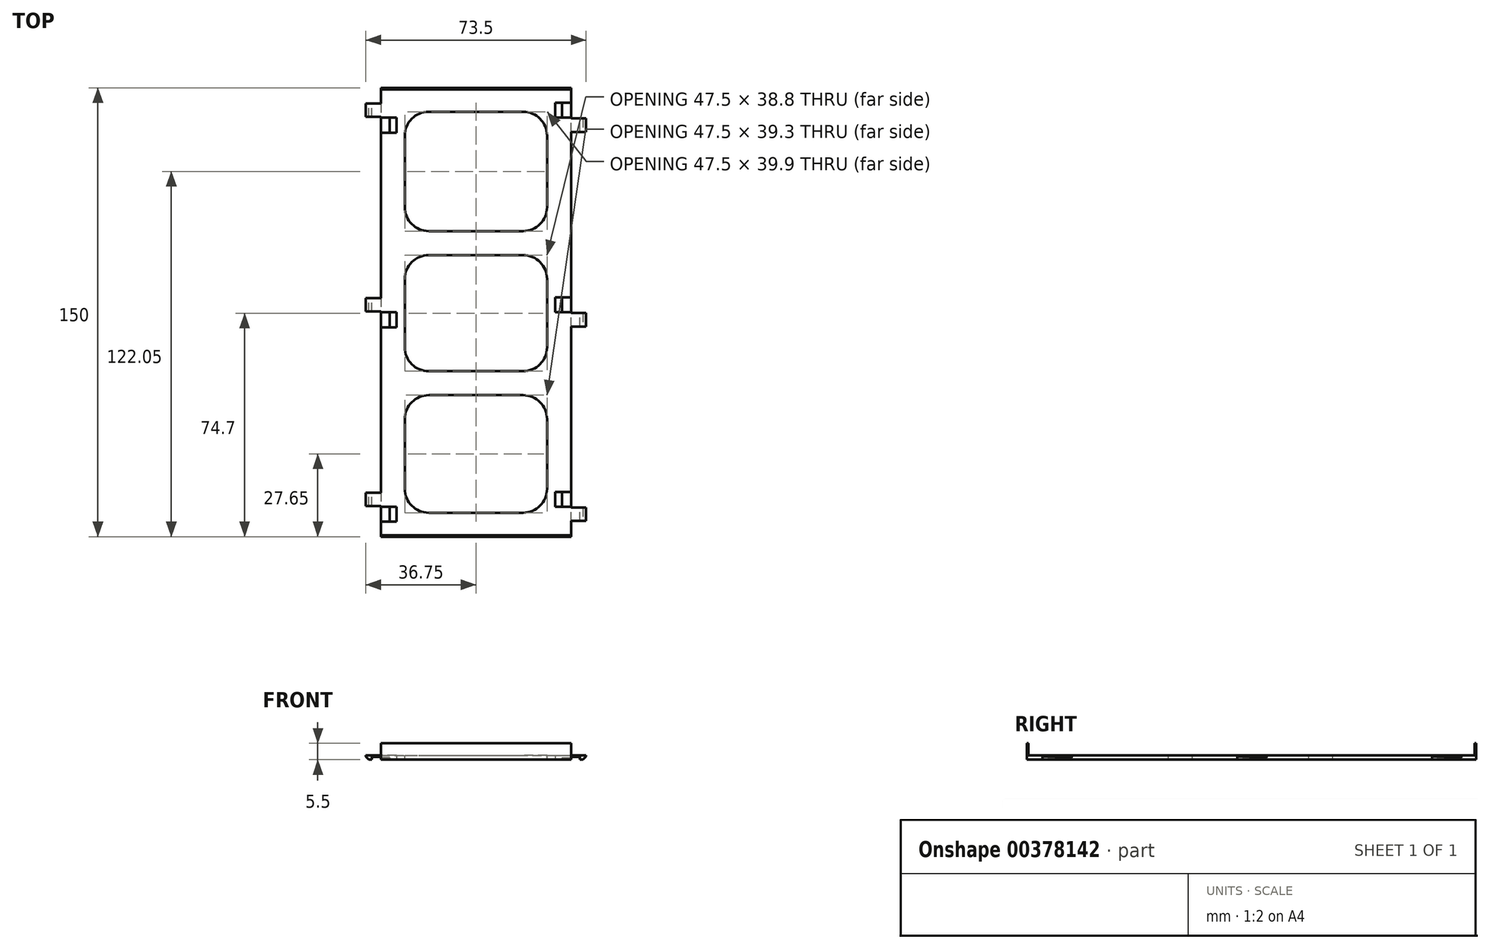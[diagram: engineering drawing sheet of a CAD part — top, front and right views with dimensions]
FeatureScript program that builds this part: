
annotation { "Feature Type Name" : "Feature", "Feature Type Description" : "" }
export const myFeature = defineFeature(function(context is Context, id is Id, definition is map)
    precondition{}
    {
        {
            var Q0;
            Q0=qCreatedBy(makeId("Top.planeOp"),FACE);
            var sketch = newSketch(context, id + "F0", { "sketchPlane" : qUnion([Q0])});
            skLineSegment(sketch, "E0.bottom", {"start": v(0, 0) * mm, "end": v(63.5, 0) * mm});
            skLineSegment(sketch, "E0.top", {"start": v(0, 150) * mm, "end": v(63.5, 150) * mm});
            skLineSegment(sketch, "E0.left", {"start": v(0, 0) * mm, "end": v(0, 150) * mm});
            skLineSegment(sketch, "E0.right", {"start": v(63.5, 0) * mm, "end": v(63.5, 150) * mm});
            skSolve(sketch);
        }
        {
            var Q0;
            Q0=qSketchRegion(id+"F0",true);
            extrude(context, id + "F1", {"entities" : qUnion([Q0]), "depth" : 1.5 * mm});
        }
        {
            var Q0;
            Q0=makeQuery(id+"F1.opExtrude","CAP_FACE",FACE,{"disambiguationData":[OSD([sQuery(id+"F0.wireOp",EDGE,"E0.bottom"),sQuery(id+"F0.wireOp",EDGE,"E0.top"),sQuery(id+"F0.wireOp",EDGE,"E0.left"),sQuery(id+"F0.wireOp",EDGE,"E0.right")])],"isStart":false});
            var sketch = newSketch(context, id + "F2", { "sketchPlane" : qUnion([Q0])});
            skLineSegment(sketch, "E1.bottom", {"start": v(8, 8) * mm, "end": v(55.5, 8) * mm});
            skLineSegment(sketch, "E1.top", {"start": v(8, 47.3) * mm, "end": v(55.5, 47.3) * mm});
            skLineSegment(sketch, "E1.left", {"start": v(8, 8) * mm, "end": v(8, 47.3) * mm});
            skLineSegment(sketch, "E1.right", {"start": v(55.5, 8) * mm, "end": v(55.5, 47.3) * mm});
            skLineSegment(sketch, "E2.bottom", {"start": v(8, 142) * mm, "end": v(55.5, 142) * mm});
            skLineSegment(sketch, "E2.top", {"start": v(8, 102.1) * mm, "end": v(55.5, 102.1) * mm});
            skLineSegment(sketch, "E2.left", {"start": v(8, 142) * mm, "end": v(8, 102.1) * mm});
            skLineSegment(sketch, "E2.right", {"start": v(55.5, 142) * mm, "end": v(55.5, 102.1) * mm});
            skLineSegment(sketch, "E3.bottom", {"start": v(8, 94.1) * mm, "end": v(55.5, 94.1) * mm});
            skLineSegment(sketch, "E3.top", {"start": v(8, 55.3) * mm, "end": v(55.5, 55.3) * mm});
            skLineSegment(sketch, "E3.left", {"start": v(8, 94.1) * mm, "end": v(8, 55.3) * mm});
            skLineSegment(sketch, "E3.right", {"start": v(55.5, 94.1) * mm, "end": v(55.5, 55.3) * mm});
            skSolve(sketch);
        }
        {
            var Q0;
            Q0=makeQuery(id+"F2.imprint","IMPRINT",FACE,{"disambiguationData":[TD([[makeQuery(id+"F2.imprint","IMPRINT",EDGE,{"derivedFrom":sQuery(id+"F2.wireOp",EDGE,"E2.bottom")}),-1.0]])]});
            var Q1;
            Q1=makeQuery(id+"F2.imprint","IMPRINT",FACE,{"disambiguationData":[TD([[makeQuery(id+"F2.imprint","IMPRINT",EDGE,{"derivedFrom":sQuery(id+"F2.wireOp",EDGE,"E3.bottom")}),-1.0]])]});
            var Q2;
            Q2=makeQuery(id+"F2.imprint","IMPRINT",FACE,{"disambiguationData":[TD([[makeQuery(id+"F2.imprint","IMPRINT",EDGE,{"derivedFrom":sQuery(id+"F2.wireOp",EDGE,"E1.bottom")}),1.0]])]});
            extrude(context, id + "F3", {"entities" : qUnion([Q0, Q1, Q2]), "operationType" : NewBodyOperationType.REMOVE, "endBound" : BoundingType.THROUGH_ALL, "oppositeDirection" : true, "depth" : 25 * mm});
        }
        {
            var Q0;
            Q0=makeQuery(id+"F3.boolean.opBoolean","COPY",EDGE,{"derivedFrom":makeQuery(id+"F3.opExtrude","SWEPT_EDGE",EDGE,{"disambiguationData":[OSD([sQuery(id+"F2.wireOp",EDGE,"E2.bottom"),sQuery(id+"F2.wireOp",EDGE,"E2.left")])]})});
            var Q1;
            Q1=makeQuery(id+"F3.boolean.opBoolean","COPY",EDGE,{"derivedFrom":makeQuery(id+"F3.opExtrude","SWEPT_EDGE",EDGE,{"disambiguationData":[OSD([sQuery(id+"F2.wireOp",EDGE,"E3.bottom"),sQuery(id+"F2.wireOp",EDGE,"E3.left")])]})});
            var Q2;
            Q2=makeQuery(id+"F3.boolean.opBoolean","COPY",EDGE,{"derivedFrom":makeQuery(id+"F3.opExtrude","SWEPT_EDGE",EDGE,{"disambiguationData":[OSD([sQuery(id+"F2.wireOp",EDGE,"E1.top"),sQuery(id+"F2.wireOp",EDGE,"E1.left")])]})});
            var Q3;
            Q3=makeQuery(id+"F3.boolean.opBoolean","COPY",EDGE,{"derivedFrom":makeQuery(id+"F3.opExtrude","SWEPT_EDGE",EDGE,{"disambiguationData":[OSD([sQuery(id+"F2.wireOp",EDGE,"E2.top"),sQuery(id+"F2.wireOp",EDGE,"E2.left")])]})});
            var Q4;
            Q4=makeQuery(id+"F3.boolean.opBoolean","COPY",EDGE,{"derivedFrom":makeQuery(id+"F3.opExtrude","SWEPT_EDGE",EDGE,{"disambiguationData":[OSD([sQuery(id+"F2.wireOp",EDGE,"E3.top"),sQuery(id+"F2.wireOp",EDGE,"E3.left")])]})});
            var Q5;
            Q5=makeQuery(id+"F3.boolean.opBoolean","COPY",EDGE,{"derivedFrom":makeQuery(id+"F3.opExtrude","SWEPT_EDGE",EDGE,{"disambiguationData":[OSD([sQuery(id+"F2.wireOp",EDGE,"E1.bottom"),sQuery(id+"F2.wireOp",EDGE,"E1.left")])]})});
            var Q6;
            Q6=makeQuery(id+"F3.boolean.opBoolean","COPY",EDGE,{"derivedFrom":makeQuery(id+"F3.opExtrude","SWEPT_EDGE",EDGE,{"disambiguationData":[OSD([sQuery(id+"F2.wireOp",EDGE,"E2.top"),sQuery(id+"F2.wireOp",EDGE,"E2.right")])]})});
            var Q7;
            Q7=makeQuery(id+"F3.boolean.opBoolean","COPY",EDGE,{"derivedFrom":makeQuery(id+"F3.opExtrude","SWEPT_EDGE",EDGE,{"disambiguationData":[OSD([sQuery(id+"F2.wireOp",EDGE,"E3.top"),sQuery(id+"F2.wireOp",EDGE,"E3.right")])]})});
            var Q8;
            Q8=makeQuery(id+"F3.boolean.opBoolean","COPY",EDGE,{"derivedFrom":makeQuery(id+"F3.opExtrude","SWEPT_EDGE",EDGE,{"disambiguationData":[OSD([sQuery(id+"F2.wireOp",EDGE,"E1.bottom"),sQuery(id+"F2.wireOp",EDGE,"E1.right")])]})});
            var Q9;
            Q9=makeQuery(id+"F3.boolean.opBoolean","COPY",EDGE,{"derivedFrom":makeQuery(id+"F3.opExtrude","SWEPT_EDGE",EDGE,{"disambiguationData":[OSD([sQuery(id+"F2.wireOp",EDGE,"E2.bottom"),sQuery(id+"F2.wireOp",EDGE,"E2.right")])]})});
            var Q10;
            Q10=makeQuery(id+"F3.boolean.opBoolean","COPY",EDGE,{"derivedFrom":makeQuery(id+"F3.opExtrude","SWEPT_EDGE",EDGE,{"disambiguationData":[OSD([sQuery(id+"F2.wireOp",EDGE,"E3.bottom"),sQuery(id+"F2.wireOp",EDGE,"E3.right")])]})});
            var Q11;
            Q11=makeQuery(id+"F3.boolean.opBoolean","COPY",EDGE,{"derivedFrom":makeQuery(id+"F3.opExtrude","SWEPT_EDGE",EDGE,{"disambiguationData":[OSD([sQuery(id+"F2.wireOp",EDGE,"E1.top"),sQuery(id+"F2.wireOp",EDGE,"E1.right")])]})});
            fillet(context, id + "F4", {"entities" : qUnion([Q0, Q1, Q2, Q3, Q4, Q5, Q6, Q7, Q8, Q9, Q10, Q11]), "radius" : 8 * mm, "tangentPropagation" : true, "allowEdgeOverflow" : false});
        }
        {
            var Q0;
            Q0=makeQuery(id+"F1.opExtrude","CAP_FACE",FACE,{"disambiguationData":[OSD([sQuery(id+"F0.wireOp",EDGE,"E0.bottom"),sQuery(id+"F0.wireOp",EDGE,"E0.top"),sQuery(id+"F0.wireOp",EDGE,"E0.left"),sQuery(id+"F0.wireOp",EDGE,"E0.right")])],"isStart":false});
            var sketch = newSketch(context, id + "F5", { "sketchPlane" : qUnion([Q0])});
            skLineSegment(sketch, "E4.bottom", {"start": v(0, 150) * mm, "end": v(63.5, 150) * mm});
            skLineSegment(sketch, "E4.top", {"start": v(0, 149.5) * mm, "end": v(63.5, 149.5) * mm});
            skLineSegment(sketch, "E4.left", {"start": v(0, 150) * mm, "end": v(0, 149.5) * mm});
            skLineSegment(sketch, "E4.right", {"start": v(63.5, 150) * mm, "end": v(63.5, 149.5) * mm});
            skLineSegment(sketch, "E5.bottom", {"start": v(0, 0) * mm, "end": v(63.5, 0) * mm});
            skLineSegment(sketch, "E5.top", {"start": v(0, 0.5) * mm, "end": v(63.5, 0.5) * mm});
            skLineSegment(sketch, "E5.left", {"start": v(0, 0) * mm, "end": v(0, 0.5) * mm});
            skLineSegment(sketch, "E5.right", {"start": v(63.5, 0) * mm, "end": v(63.5, 0.5) * mm});
            skSolve(sketch);
        }
        {
            var Q0;
            Q0=makeQuery(id+"F5.imprint","IMPRINT",FACE,{"disambiguationData":[TD([[makeQuery(id+"F5.imprint","IMPRINT",EDGE,{"derivedFrom":sQuery(id+"F5.wireOp",EDGE,"E5.bottom")}),1.0]])]});
            var Q1;
            Q1=makeQuery(id+"F5.imprint","IMPRINT",FACE,{"disambiguationData":[TD([[makeQuery(id+"F5.imprint","IMPRINT",EDGE,{"derivedFrom":sQuery(id+"F5.wireOp",EDGE,"E4.bottom")}),-1.0]])]});
            extrude(context, id + "F6", {"entities" : qUnion([Q0, Q1]), "operationType" : NewBodyOperationType.ADD, "depth" : 4 * mm});
        }
        {
            var Q0;
            Q0=makeQuery(id+"F6.boolean.opBoolean","MERGE",FACE,{"derivedFrom":[makeQuery(id+"F1.opExtrude","SWEPT_FACE",FACE,{"disambiguationData":[OSD([sQuery(id+"F0.wireOp",EDGE,"E0.right")])]}),makeQuery(id+"F6.opExtrude","SWEPT_FACE",FACE,{"disambiguationData":[OSD([sQuery(id+"F5.wireOp",EDGE,"E4.right")])]}),makeQuery(id+"F6.opExtrude","SWEPT_FACE",FACE,{"disambiguationData":[OSD([sQuery(id+"F5.wireOp",EDGE,"E5.right")])]})]});
            var sketch = newSketch(context, id + "F7", { "sketchPlane" : qUnion([Q0])});
            skLineSegment(sketch, "E6.bottom", {"start": v(10, 1.5) * mm, "end": v(15, 1.5) * mm});
            skLineSegment(sketch, "E6.top", {"start": v(10, 0.7) * mm, "end": v(15, 0.7) * mm});
            skLineSegment(sketch, "E6.left", {"start": v(10, 1.5) * mm, "end": v(10, 0.7) * mm});
            skLineSegment(sketch, "E6.right", {"start": v(15, 1.5) * mm, "end": v(15, 0.7) * mm});
            skLineSegment(sketch, "E7.bottom", {"start": v(75, 1.5) * mm, "end": v(80, 1.5) * mm});
            skLineSegment(sketch, "E7.top", {"start": v(75, 0.7) * mm, "end": v(80, 0.7) * mm});
            skLineSegment(sketch, "E7.left", {"start": v(75, 1.5) * mm, "end": v(75, 0.7) * mm});
            skLineSegment(sketch, "E7.right", {"start": v(80, 1.5) * mm, "end": v(80, 0.7) * mm});
            skLineSegment(sketch, "E8.bottom", {"start": v(140, 1.5) * mm, "end": v(145, 1.5) * mm});
            skLineSegment(sketch, "E8.top", {"start": v(140, 0.7) * mm, "end": v(145, 0.7) * mm});
            skLineSegment(sketch, "E8.left", {"start": v(140, 1.5) * mm, "end": v(140, 0.7) * mm});
            skLineSegment(sketch, "E8.right", {"start": v(145, 1.5) * mm, "end": v(145, 0.7) * mm});
            skSolve(sketch);
        }
        {
            var Q0;
            Q0=makeQuery(id+"F7.imprint","IMPRINT",FACE,{"disambiguationData":[TD([[makeQuery(id+"F7.imprint","IMPRINT",EDGE,{"derivedFrom":sQuery(id+"F7.wireOp",EDGE,"E8.bottom")}),-1.0]])]});
            var Q1;
            Q1=makeQuery(id+"F7.imprint","IMPRINT",FACE,{"disambiguationData":[TD([[makeQuery(id+"F7.imprint","IMPRINT",EDGE,{"derivedFrom":sQuery(id+"F7.wireOp",EDGE,"E7.bottom")}),-1.0]])]});
            var Q2;
            Q2=makeQuery(id+"F7.imprint","IMPRINT",FACE,{"disambiguationData":[TD([[makeQuery(id+"F7.imprint","IMPRINT",EDGE,{"derivedFrom":sQuery(id+"F7.wireOp",EDGE,"E6.bottom")}),-1.0]])]});
            extrude(context, id + "F8", {"entities" : qUnion([Q0, Q1, Q2]), "operationType" : NewBodyOperationType.REMOVE, "oppositeDirection" : true, "depth" : 5.25 * mm});
        }
        {
            var Q0;
            Q0=makeQuery(id+"F6.boolean.opBoolean","MERGE",FACE,{"derivedFrom":[makeQuery(id+"F1.opExtrude","SWEPT_FACE",FACE,{"disambiguationData":[OSD([sQuery(id+"F0.wireOp",EDGE,"E0.left")])]}),makeQuery(id+"F6.opExtrude","SWEPT_FACE",FACE,{"disambiguationData":[OSD([sQuery(id+"F5.wireOp",EDGE,"E4.left")])]}),makeQuery(id+"F6.opExtrude","SWEPT_FACE",FACE,{"disambiguationData":[OSD([sQuery(id+"F5.wireOp",EDGE,"E5.left")])]})]});
            var sketch = newSketch(context, id + "F9", { "sketchPlane" : qUnion([Q0])});
            skLineSegment(sketch, "E9.bottom", {"start": v(-140, 1.5) * mm, "end": v(-135, 1.5) * mm});
            skLineSegment(sketch, "E9.top", {"start": v(-140, 0.7) * mm, "end": v(-135, 0.7) * mm});
            skLineSegment(sketch, "E9.left", {"start": v(-140, 1.5) * mm, "end": v(-140, 0.7) * mm});
            skLineSegment(sketch, "E9.right", {"start": v(-135, 1.5) * mm, "end": v(-135, 0.7) * mm});
            skLineSegment(sketch, "E10.bottom", {"start": v(-75, 1.5) * mm, "end": v(-70, 1.5) * mm});
            skLineSegment(sketch, "E10.top", {"start": v(-75, 0.7) * mm, "end": v(-70, 0.7) * mm});
            skLineSegment(sketch, "E10.left", {"start": v(-75, 1.5) * mm, "end": v(-75, 0.7) * mm});
            skLineSegment(sketch, "E10.right", {"start": v(-70, 1.5) * mm, "end": v(-70, 0.7) * mm});
            skLineSegment(sketch, "E11.bottom", {"start": v(-10, 1.5) * mm, "end": v(-5, 1.5) * mm});
            skLineSegment(sketch, "E11.top", {"start": v(-10, 0.7) * mm, "end": v(-5, 0.7) * mm});
            skLineSegment(sketch, "E11.left", {"start": v(-10, 1.5) * mm, "end": v(-10, 0.7) * mm});
            skLineSegment(sketch, "E11.right", {"start": v(-5, 1.5) * mm, "end": v(-5, 0.7) * mm});
            skSolve(sketch);
        }
        {
            var Q0;
            Q0=makeQuery(id+"F9.imprint","IMPRINT",FACE,{"disambiguationData":[TD([[makeQuery(id+"F9.imprint","IMPRINT",EDGE,{"derivedFrom":sQuery(id+"F9.wireOp",EDGE,"E11.bottom")}),1.0]])]});
            var Q1;
            Q1=makeQuery(id+"F9.imprint","IMPRINT",FACE,{"disambiguationData":[TD([[makeQuery(id+"F9.imprint","IMPRINT",EDGE,{"derivedFrom":sQuery(id+"F9.wireOp",EDGE,"E10.bottom")}),1.0]])]});
            var Q2;
            Q2=makeQuery(id+"F9.imprint","IMPRINT",FACE,{"disambiguationData":[TD([[makeQuery(id+"F9.imprint","IMPRINT",EDGE,{"derivedFrom":sQuery(id+"F9.wireOp",EDGE,"E9.bottom")}),1.0]])]});
            extrude(context, id + "F10", {"entities" : qUnion([Q0, Q1, Q2]), "operationType" : NewBodyOperationType.REMOVE, "oppositeDirection" : true, "depth" : 5.25 * mm});
        }
        {
            var Q0;
            Q0=makeQuery(id+"F6.boolean.opBoolean","MERGE",FACE,{"derivedFrom":[makeQuery(id+"F1.opExtrude","SWEPT_FACE",FACE,{"disambiguationData":[OSD([sQuery(id+"F0.wireOp",EDGE,"E0.left")])]}),makeQuery(id+"F6.opExtrude","SWEPT_FACE",FACE,{"disambiguationData":[OSD([sQuery(id+"F5.wireOp",EDGE,"E4.left")])]}),makeQuery(id+"F6.opExtrude","SWEPT_FACE",FACE,{"disambiguationData":[OSD([sQuery(id+"F5.wireOp",EDGE,"E5.left")])]})]});
            var sketch = newSketch(context, id + "F11", { "sketchPlane" : qUnion([Q0])});
            skLineSegment(sketch, "E12.bottom", {"start": v(-144.75, 1.5) * mm, "end": v(-140.25, 1.5) * mm});
            skLineSegment(sketch, "E12.top", {"start": v(-144.75, 0.9) * mm, "end": v(-140.25, 0.9) * mm});
            skLineSegment(sketch, "E12.left", {"start": v(-144.75, 1.5) * mm, "end": v(-144.75, 0.9) * mm});
            skLineSegment(sketch, "E12.right", {"start": v(-140.25, 1.5) * mm, "end": v(-140.25, 0.9) * mm});
            skLineSegment(sketch, "E13.bottom", {"start": v(-79.75, 1.5) * mm, "end": v(-75.25, 1.5) * mm});
            skLineSegment(sketch, "E13.top", {"start": v(-79.75, 0.9) * mm, "end": v(-75.25, 0.9) * mm});
            skLineSegment(sketch, "E13.left", {"start": v(-79.75, 1.5) * mm, "end": v(-79.75, 0.9) * mm});
            skLineSegment(sketch, "E13.right", {"start": v(-75.25, 1.5) * mm, "end": v(-75.25, 0.9) * mm});
            skLineSegment(sketch, "E14.bottom", {"start": v(-14.75, 1.5) * mm, "end": v(-10.25, 1.5) * mm});
            skLineSegment(sketch, "E14.top", {"start": v(-14.75, 0.9) * mm, "end": v(-10.25, 0.9) * mm});
            skLineSegment(sketch, "E14.left", {"start": v(-14.75, 1.5) * mm, "end": v(-14.75, 0.9) * mm});
            skLineSegment(sketch, "E14.right", {"start": v(-10.25, 1.5) * mm, "end": v(-10.25, 0.9) * mm});
            skSolve(sketch);
        }
        {
            var Q0;
            Q0=makeQuery(id+"F11.imprint","IMPRINT",FACE,{"disambiguationData":[TD([[makeQuery(id+"F11.imprint","IMPRINT",EDGE,{"derivedFrom":sQuery(id+"F11.wireOp",EDGE,"E12.bottom")}),1.0]])]});
            var Q1;
            Q1=makeQuery(id+"F11.imprint","IMPRINT",FACE,{"disambiguationData":[TD([[makeQuery(id+"F11.imprint","IMPRINT",EDGE,{"derivedFrom":sQuery(id+"F11.wireOp",EDGE,"E13.bottom")}),1.0]])]});
            var Q2;
            Q2=makeQuery(id+"F11.imprint","IMPRINT",FACE,{"disambiguationData":[TD([[makeQuery(id+"F11.imprint","IMPRINT",EDGE,{"derivedFrom":sQuery(id+"F11.wireOp",EDGE,"E14.bottom")}),1.0]])]});
            extrude(context, id + "F12", {"entities" : qUnion([Q0, Q1, Q2]), "operationType" : NewBodyOperationType.ADD, "depth" : 5 * mm});
        }
        {
            var Q0;
            Q0=makeQuery(id+"F6.boolean.opBoolean","MERGE",FACE,{"derivedFrom":[makeQuery(id+"F1.opExtrude","SWEPT_FACE",FACE,{"disambiguationData":[OSD([sQuery(id+"F0.wireOp",EDGE,"E0.right")])]}),makeQuery(id+"F6.opExtrude","SWEPT_FACE",FACE,{"disambiguationData":[OSD([sQuery(id+"F5.wireOp",EDGE,"E4.right")])]}),makeQuery(id+"F6.opExtrude","SWEPT_FACE",FACE,{"disambiguationData":[OSD([sQuery(id+"F5.wireOp",EDGE,"E5.right")])]})]});
            var sketch = newSketch(context, id + "F13", { "sketchPlane" : qUnion([Q0])});
            skLineSegment(sketch, "E15.bottom", {"start": v(5.25, 1.5) * mm, "end": v(9.75, 1.5) * mm});
            skLineSegment(sketch, "E15.top", {"start": v(5.25, 0.9) * mm, "end": v(9.75, 0.9) * mm});
            skLineSegment(sketch, "E15.left", {"start": v(5.25, 1.5) * mm, "end": v(5.25, 0.9) * mm});
            skLineSegment(sketch, "E15.right", {"start": v(9.75, 1.5) * mm, "end": v(9.75, 0.9) * mm});
            skLineSegment(sketch, "E16.bottom", {"start": v(70.25, 1.5) * mm, "end": v(74.75, 1.5) * mm});
            skLineSegment(sketch, "E16.top", {"start": v(70.25, 0.9) * mm, "end": v(74.75, 0.9) * mm});
            skLineSegment(sketch, "E16.left", {"start": v(70.25, 1.5) * mm, "end": v(70.25, 0.9) * mm});
            skLineSegment(sketch, "E16.right", {"start": v(74.75, 1.5) * mm, "end": v(74.75, 0.9) * mm});
            skLineSegment(sketch, "E17.bottom", {"start": v(135.25, 1.5) * mm, "end": v(139.75, 1.5) * mm});
            skLineSegment(sketch, "E17.top", {"start": v(135.25, 0.9) * mm, "end": v(139.75, 0.9) * mm});
            skLineSegment(sketch, "E17.left", {"start": v(135.25, 1.5) * mm, "end": v(135.25, 0.9) * mm});
            skLineSegment(sketch, "E17.right", {"start": v(139.75, 1.5) * mm, "end": v(139.75, 0.9) * mm});
            skSolve(sketch);
        }
        {
            var Q0;
            Q0=makeQuery(id+"F13.imprint","IMPRINT",FACE,{"disambiguationData":[TD([[makeQuery(id+"F13.imprint","IMPRINT",EDGE,{"derivedFrom":sQuery(id+"F13.wireOp",EDGE,"E17.bottom")}),-1.0]])]});
            var Q1;
            Q1=makeQuery(id+"F13.imprint","IMPRINT",FACE,{"disambiguationData":[TD([[makeQuery(id+"F13.imprint","IMPRINT",EDGE,{"derivedFrom":sQuery(id+"F13.wireOp",EDGE,"E16.bottom")}),-1.0]])]});
            var Q2;
            Q2=makeQuery(id+"F13.imprint","IMPRINT",FACE,{"disambiguationData":[TD([[makeQuery(id+"F13.imprint","IMPRINT",EDGE,{"derivedFrom":sQuery(id+"F13.wireOp",EDGE,"E15.bottom")}),-1.0]])]});
            extrude(context, id + "F14", {"entities" : qUnion([Q0, Q1, Q2]), "operationType" : NewBodyOperationType.ADD, "depth" : 5 * mm});
        }
        {
            var Q0;
            Q0=makeQuery(id+"F1.opExtrude","CAP_FACE",FACE,{"disambiguationData":[OSD([sQuery(id+"F0.wireOp",EDGE,"E0.bottom"),sQuery(id+"F0.wireOp",EDGE,"E0.top"),sQuery(id+"F0.wireOp",EDGE,"E0.left"),sQuery(id+"F0.wireOp",EDGE,"E0.right")])],"isStart":true});
            var sketch = newSketch(context, id + "F15", { "sketchPlane" : qUnion([Q0])});
            skLineSegment(sketch, "E18.bottom", {"start": v(58.25, -15) * mm, "end": v(60.5, -15) * mm});
            skLineSegment(sketch, "E18.top", {"start": v(58.25, -10) * mm, "end": v(60.5, -10) * mm});
            skLineSegment(sketch, "E18.left", {"start": v(58.25, -15) * mm, "end": v(58.25, -10) * mm});
            skLineSegment(sketch, "E18.right", {"start": v(60.5, -15) * mm, "end": v(60.5, -10) * mm});
            skLineSegment(sketch, "E19.bottom", {"start": v(58.25, -80) * mm, "end": v(60.5, -80) * mm});
            skLineSegment(sketch, "E19.top", {"start": v(58.25, -75) * mm, "end": v(60.5, -75) * mm});
            skLineSegment(sketch, "E19.left", {"start": v(58.25, -80) * mm, "end": v(58.25, -75) * mm});
            skLineSegment(sketch, "E19.right", {"start": v(60.5, -80) * mm, "end": v(60.5, -75) * mm});
            skLineSegment(sketch, "E20.bottom", {"start": v(58.25, -145) * mm, "end": v(60.5, -145) * mm});
            skLineSegment(sketch, "E20.top", {"start": v(58.25, -140) * mm, "end": v(60.5, -140) * mm});
            skLineSegment(sketch, "E20.left", {"start": v(58.25, -145) * mm, "end": v(58.25, -140) * mm});
            skLineSegment(sketch, "E20.right", {"start": v(60.5, -145) * mm, "end": v(60.5, -140) * mm});
            skLineSegment(sketch, "E21.bottom", {"start": v(5.25, -140) * mm, "end": v(3, -140) * mm});
            skLineSegment(sketch, "E21.top", {"start": v(5.25, -135) * mm, "end": v(3, -135) * mm});
            skLineSegment(sketch, "E21.left", {"start": v(5.25, -140) * mm, "end": v(5.25, -135) * mm});
            skLineSegment(sketch, "E21.right", {"start": v(3, -140) * mm, "end": v(3, -135) * mm});
            skLineSegment(sketch, "E22.bottom", {"start": v(5.25, -75) * mm, "end": v(3, -75) * mm});
            skLineSegment(sketch, "E22.top", {"start": v(5.25, -70) * mm, "end": v(3, -70) * mm});
            skLineSegment(sketch, "E22.left", {"start": v(5.25, -75) * mm, "end": v(5.25, -70) * mm});
            skLineSegment(sketch, "E22.right", {"start": v(3, -75) * mm, "end": v(3, -70) * mm});
            skLineSegment(sketch, "E23.bottom", {"start": v(5.25, -10) * mm, "end": v(3, -10) * mm});
            skLineSegment(sketch, "E23.top", {"start": v(5.25, -5) * mm, "end": v(3, -5) * mm});
            skLineSegment(sketch, "E23.left", {"start": v(5.25, -10) * mm, "end": v(5.25, -5) * mm});
            skLineSegment(sketch, "E23.right", {"start": v(3, -10) * mm, "end": v(3, -5) * mm});
            skSolve(sketch);
        }
        {
            var Q0;
            Q0=makeQuery(id+"F15.imprint","IMPRINT",FACE,{"disambiguationData":[TD([[makeQuery(id+"F15.imprint","IMPRINT",EDGE,{"derivedFrom":sQuery(id+"F15.wireOp",EDGE,"E18.bottom")}),1.0]])]});
            var Q1;
            Q1=makeQuery(id+"F15.imprint","IMPRINT",FACE,{"disambiguationData":[TD([[makeQuery(id+"F15.imprint","IMPRINT",EDGE,{"derivedFrom":sQuery(id+"F15.wireOp",EDGE,"E23.bottom")}),-1.0]])]});
            var Q2;
            Q2=makeQuery(id+"F15.imprint","IMPRINT",FACE,{"disambiguationData":[TD([[makeQuery(id+"F15.imprint","IMPRINT",EDGE,{"derivedFrom":sQuery(id+"F15.wireOp",EDGE,"E19.bottom")}),1.0]])]});
            var Q3;
            Q3=makeQuery(id+"F15.imprint","IMPRINT",FACE,{"disambiguationData":[TD([[makeQuery(id+"F15.imprint","IMPRINT",EDGE,{"derivedFrom":sQuery(id+"F15.wireOp",EDGE,"E22.bottom")}),-1.0]])]});
            var Q4;
            Q4=makeQuery(id+"F15.imprint","IMPRINT",FACE,{"disambiguationData":[TD([[makeQuery(id+"F15.imprint","IMPRINT",EDGE,{"derivedFrom":sQuery(id+"F15.wireOp",EDGE,"E20.bottom")}),1.0]])]});
            var Q5;
            Q5=makeQuery(id+"F15.imprint","IMPRINT",FACE,{"disambiguationData":[TD([[makeQuery(id+"F15.imprint","IMPRINT",EDGE,{"derivedFrom":sQuery(id+"F15.wireOp",EDGE,"E21.bottom")}),-1.0]])]});
            extrude(context, id + "F16", {"entities" : qUnion([Q0, Q1, Q2, Q3, Q4, Q5]), "operationType" : NewBodyOperationType.REMOVE, "endBound" : BoundingType.THROUGH_ALL, "oppositeDirection" : true, "depth" : 25 * mm});
        }
        {
            var Q0;
            Q0=makeQuery(id+"F12.opExtrude","SWEPT_FACE",FACE,{"disambiguationData":[OSD([sQuery(id+"F11.wireOp",EDGE,"E14.top")])]});
            var sketch = newSketch(context, id + "F17", { "sketchPlane" : qUnion([Q0])});
            skLineSegment(sketch, "E24.bottom", {"start": v(-5, -10.25) * mm, "end": v(-3, -10.25) * mm});
            skLineSegment(sketch, "E24.top", {"start": v(-5, -14.75) * mm, "end": v(-3, -14.75) * mm});
            skLineSegment(sketch, "E24.left", {"start": v(-5, -10.25) * mm, "end": v(-5, -14.75) * mm});
            skLineSegment(sketch, "E24.right", {"start": v(-3, -10.25) * mm, "end": v(-3, -14.75) * mm});
            skSolve(sketch);
        }
        {
            var Q0;
            Q0=makeQuery(id+"F17.imprint","IMPRINT",FACE,{"disambiguationData":[TD([[makeQuery(id+"F17.imprint","IMPRINT",EDGE,{"derivedFrom":sQuery(id+"F17.wireOp",EDGE,"E24.bottom")}),-1.0]])]});
            extrude(context, id + "F18", {"entities" : qUnion([Q0]), "operationType" : NewBodyOperationType.ADD, "depth" : 0.9 * mm});
        }
        {
            var Q0;
            Q0=makeQuery(id+"F12.opExtrude","SWEPT_FACE",FACE,{"disambiguationData":[OSD([sQuery(id+"F11.wireOp",EDGE,"E13.top")])]});
            var sketch = newSketch(context, id + "F19", { "sketchPlane" : qUnion([Q0])});
            skLineSegment(sketch, "E25.bottom", {"start": v(-5, -75.25) * mm, "end": v(-3, -75.25) * mm});
            skLineSegment(sketch, "E25.top", {"start": v(-5, -79.75) * mm, "end": v(-3, -79.75) * mm});
            skLineSegment(sketch, "E25.left", {"start": v(-5, -75.25) * mm, "end": v(-5, -79.75) * mm});
            skLineSegment(sketch, "E25.right", {"start": v(-3, -75.25) * mm, "end": v(-3, -79.75) * mm});
            skSolve(sketch);
        }
        {
            var Q0;
            Q0=makeQuery(id+"F19.imprint","IMPRINT",FACE,{"disambiguationData":[TD([[makeQuery(id+"F19.imprint","IMPRINT",EDGE,{"derivedFrom":sQuery(id+"F19.wireOp",EDGE,"E25.bottom")}),-1.0]])]});
            extrude(context, id + "F20", {"entities" : qUnion([Q0]), "operationType" : NewBodyOperationType.ADD, "depth" : 0.9 * mm});
        }
        {
            var Q0;
            Q0=makeQuery(id+"F12.opExtrude","SWEPT_FACE",FACE,{"disambiguationData":[OSD([sQuery(id+"F11.wireOp",EDGE,"E12.top")])]});
            var sketch = newSketch(context, id + "F21", { "sketchPlane" : qUnion([Q0])});
            skLineSegment(sketch, "E26.bottom", {"start": v(-5, -140.25) * mm, "end": v(-3, -140.25) * mm});
            skLineSegment(sketch, "E26.top", {"start": v(-5, -144.75) * mm, "end": v(-3, -144.75) * mm});
            skLineSegment(sketch, "E26.left", {"start": v(-5, -140.25) * mm, "end": v(-5, -144.75) * mm});
            skLineSegment(sketch, "E26.right", {"start": v(-3, -140.25) * mm, "end": v(-3, -144.75) * mm});
            skSolve(sketch);
        }
        {
            var Q0;
            Q0=makeQuery(id+"F21.imprint","IMPRINT",FACE,{"disambiguationData":[TD([[makeQuery(id+"F21.imprint","IMPRINT",EDGE,{"derivedFrom":sQuery(id+"F21.wireOp",EDGE,"E26.bottom")}),-1.0]])]});
            extrude(context, id + "F22", {"entities" : qUnion([Q0]), "operationType" : NewBodyOperationType.ADD, "depth" : 0.9 * mm});
        }
        {
            var Q0;
            Q0=makeQuery(id+"F14.opExtrude","SWEPT_FACE",FACE,{"disambiguationData":[OSD([sQuery(id+"F13.wireOp",EDGE,"E17.top")])]});
            var sketch = newSketch(context, id + "F23", { "sketchPlane" : qUnion([Q0])});
            skLineSegment(sketch, "E27.bottom", {"start": v(68.5, -135.25) * mm, "end": v(66.5, -135.25) * mm});
            skLineSegment(sketch, "E27.top", {"start": v(68.5, -139.75) * mm, "end": v(66.5, -139.75) * mm});
            skLineSegment(sketch, "E27.left", {"start": v(68.5, -135.25) * mm, "end": v(68.5, -139.75) * mm});
            skLineSegment(sketch, "E27.right", {"start": v(66.5, -135.25) * mm, "end": v(66.5, -139.75) * mm});
            skSolve(sketch);
        }
        {
            var Q0;
            Q0=makeQuery(id+"F23.imprint","IMPRINT",FACE,{"disambiguationData":[TD([[makeQuery(id+"F23.imprint","IMPRINT",EDGE,{"derivedFrom":sQuery(id+"F23.wireOp",EDGE,"E27.bottom")}),1.0]])]});
            extrude(context, id + "F24", {"entities" : qUnion([Q0]), "operationType" : NewBodyOperationType.ADD, "depth" : 0.9 * mm});
        }
        {
            var Q0;
            Q0=makeQuery(id+"F14.opExtrude","SWEPT_FACE",FACE,{"disambiguationData":[OSD([sQuery(id+"F13.wireOp",EDGE,"E16.top")])]});
            var sketch = newSketch(context, id + "F25", { "sketchPlane" : qUnion([Q0])});
            skLineSegment(sketch, "E28.bottom", {"start": v(68.5, -70.25) * mm, "end": v(66.5, -70.25) * mm});
            skLineSegment(sketch, "E28.top", {"start": v(68.5, -74.75) * mm, "end": v(66.5, -74.75) * mm});
            skLineSegment(sketch, "E28.left", {"start": v(68.5, -70.25) * mm, "end": v(68.5, -74.75) * mm});
            skLineSegment(sketch, "E28.right", {"start": v(66.5, -70.25) * mm, "end": v(66.5, -74.75) * mm});
            skSolve(sketch);
        }
        {
            var Q0;
            Q0=makeQuery(id+"F25.imprint","IMPRINT",FACE,{"disambiguationData":[TD([[makeQuery(id+"F25.imprint","IMPRINT",EDGE,{"derivedFrom":sQuery(id+"F25.wireOp",EDGE,"E28.bottom")}),1.0]])]});
            extrude(context, id + "F26", {"entities" : qUnion([Q0]), "operationType" : NewBodyOperationType.ADD, "depth" : 0.9 * mm});
        }
        {
            var Q0;
            Q0=makeQuery(id+"F14.opExtrude","SWEPT_FACE",FACE,{"disambiguationData":[OSD([sQuery(id+"F13.wireOp",EDGE,"E15.top")])]});
            var sketch = newSketch(context, id + "F27", { "sketchPlane" : qUnion([Q0])});
            skLineSegment(sketch, "E29.bottom", {"start": v(68.5, -5.25) * mm, "end": v(66.5, -5.25) * mm});
            skLineSegment(sketch, "E29.top", {"start": v(68.5, -9.75) * mm, "end": v(66.5, -9.75) * mm});
            skLineSegment(sketch, "E29.left", {"start": v(68.5, -5.25) * mm, "end": v(68.5, -9.75) * mm});
            skLineSegment(sketch, "E29.right", {"start": v(66.5, -5.25) * mm, "end": v(66.5, -9.75) * mm});
            skSolve(sketch);
        }
        {
            var Q0;
            Q0=makeQuery(id+"F27.imprint","IMPRINT",FACE,{"disambiguationData":[TD([[makeQuery(id+"F27.imprint","IMPRINT",EDGE,{"derivedFrom":sQuery(id+"F27.wireOp",EDGE,"E29.bottom")}),1.0]])]});
            extrude(context, id + "F28", {"entities" : qUnion([Q0]), "operationType" : NewBodyOperationType.ADD, "depth" : 0.9 * mm});
        }
        {
            var Q0;
            Q0=makeQuery(id+"F22.opExtrude","CAP_EDGE",EDGE,{"disambiguationData":[OSD([sQuery(id+"F21.wireOp",EDGE,"E26.left")])],"isStart":false});
            var Q1;
            Q1=makeQuery(id+"F20.opExtrude","CAP_EDGE",EDGE,{"disambiguationData":[OSD([sQuery(id+"F19.wireOp",EDGE,"E25.left")])],"isStart":false});
            var Q2;
            Q2=makeQuery(id+"F18.opExtrude","CAP_EDGE",EDGE,{"disambiguationData":[OSD([sQuery(id+"F17.wireOp",EDGE,"E24.left")])],"isStart":false});
            var Q3;
            Q3=makeQuery(id+"F26.opExtrude","CAP_EDGE",EDGE,{"disambiguationData":[OSD([sQuery(id+"F25.wireOp",EDGE,"E28.left")])],"isStart":false});
            var Q4;
            Q4=makeQuery(id+"F24.opExtrude","CAP_EDGE",EDGE,{"disambiguationData":[OSD([sQuery(id+"F23.wireOp",EDGE,"E27.left")])],"isStart":false});
            var Q5;
            Q5=makeQuery(id+"F28.opExtrude","CAP_EDGE",EDGE,{"disambiguationData":[OSD([sQuery(id+"F27.wireOp",EDGE,"E29.left")])],"isStart":false});
            chamfer(context, id + "F29", {"entities" : qUnion([Q0, Q1, Q2, Q3, Q4, Q5]), "width" : 1 * mm, "tangentPropagation" : true});
        }
    });
